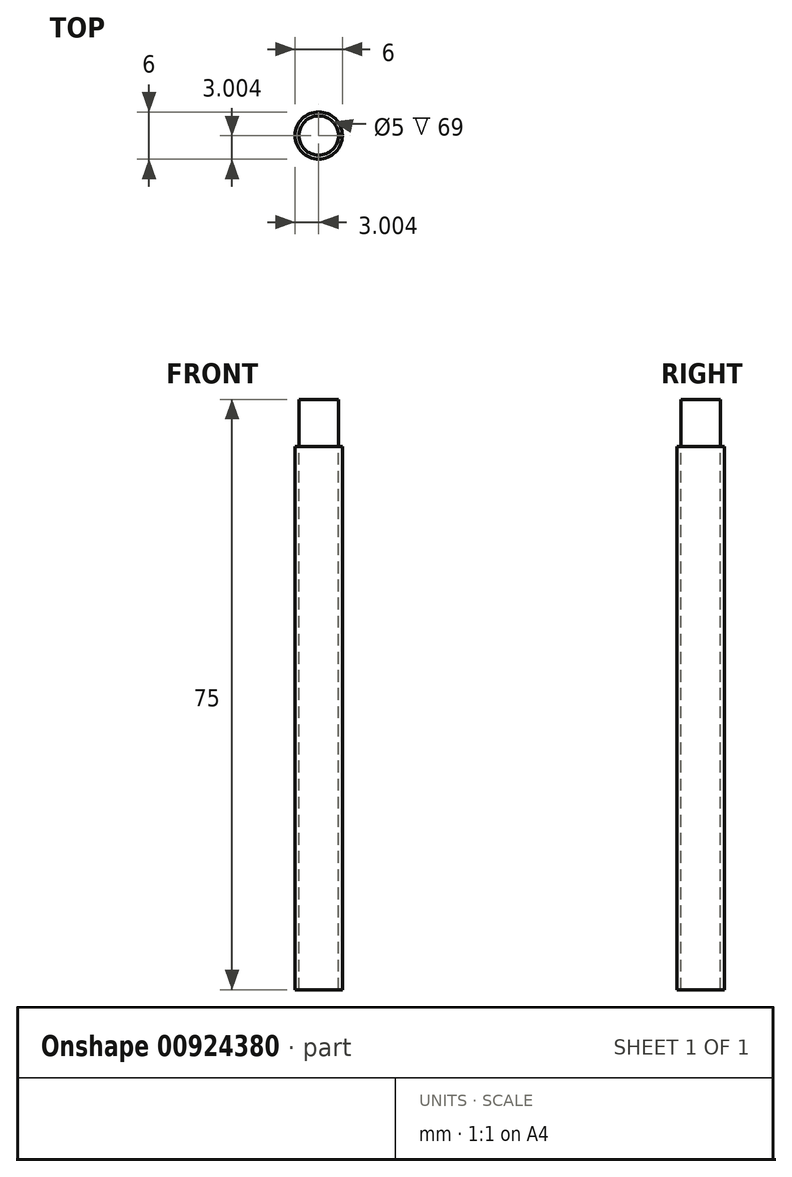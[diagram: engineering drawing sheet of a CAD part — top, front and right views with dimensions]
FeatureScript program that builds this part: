
annotation { "Feature Type Name" : "Feature", "Feature Type Description" : "" }
export const myFeature = defineFeature(function(context is Context, id is Id, definition is map)
    precondition{}
    {
        {
            var Q0;
            Q0=qCreatedBy(makeId("Top.planeOp"),FACE);
            var sketch = newSketch(context, id + "F0", { "sketchPlane" : qUnion([Q0])});
            skCircle(sketch, "E0", {"center": v(-28.22, 25.5) * mm, "radius": 2.5 * mm});
            skSolve(sketch);
        }
        {
            var Q0;
            Q0 = qSketchRegion(id + "F0", true);
            extrude(context, id + "F1", {"entities" : qUnion([Q0]), "depth" : 6 * mm, "offsetDistance" : 25 * mm});
        }
        {
            var Q0;
            Q0=makeQuery(id+"F1.opExtrude","CAP_FACE",FACE,{"disambiguationData":[OSD([sQuery(id+"F0.wireOp",EDGE,"E0")])],"isStart":true});
            var sketch = newSketch(context, id + "F2", { "sketchPlane" : qUnion([Q0])});
            skCircle(sketch, "E1", {"center": v(-28.22, -25.5) * mm, "radius": 3 * mm});
            skSolve(sketch);
        }
        {
            var Q0;
            Q0=makeQuery(id+"F2.imprint","IMPRINT",FACE,{"disambiguationData":[TD([[makeQuery(id+"F2.imprint","IMPRINT",EDGE,{"derivedFrom":sQuery(id+"F2.wireOp",EDGE,"E1")}),1.0]])]});
            extrude(context, id + "F3", {"entities" : qUnion([Q0]), "depth" : 69 * mm, "offsetDistance" : 25 * mm});
        }
    });
